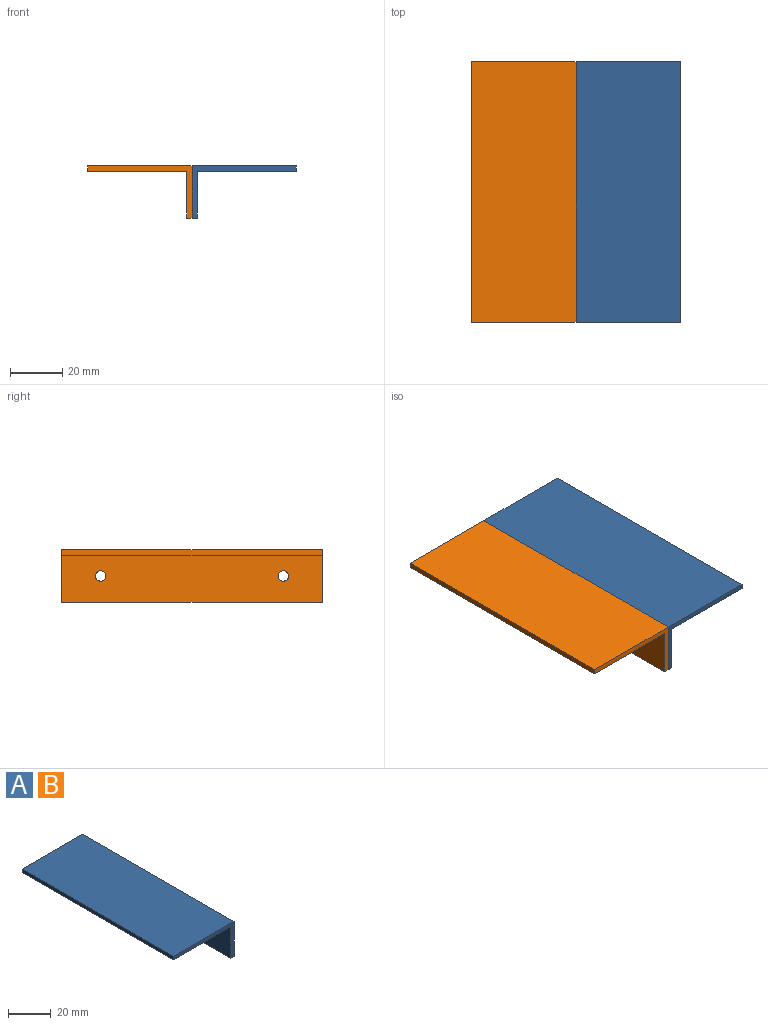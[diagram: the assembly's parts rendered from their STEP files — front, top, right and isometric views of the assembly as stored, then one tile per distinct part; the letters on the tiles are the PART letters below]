
ASSEMBLY  parts=2 mates=1
PART A: 10 faces, bbox 40x100x20 mm
  f0: plane 100x18mm, normal (-1,0,0), area 1774.9mm2, adj f3,f4,f6,f7,f8,f9
  f1: plane 100x20mm, normal (1,0,0), area 1974.9mm2, adj f4,f5,f6,f7,f8,f9
  f2: plane 100x2mm, normal (-1,0,0), area 200mm2, adj f3,f5,f6,f7
  f3: plane 100x38mm, normal (0,0,-1), area 3800mm2, adj f0,f2,f6,f7
  f4: plane 100x2mm, normal (0,0,-1), area 200mm2, adj f0,f1,f6,f7
  f5: plane 100x40mm, normal (0,0,1), area 4000mm2, adj f1,f2,f6,f7
  f6: plane 40x20mm, normal (0,-1,0), area 116mm2, adj f0,f1,f2,f3,f4,f5
  f7: plane 40x20mm, normal (0,1,0), area 116mm2, adj f0,f1,f2,f3,f4,f5
  f8: cylinder r=2mm len=4mm, axis (-1,0,0), area 25.1mm2, adj f0,f1
  f9: cylinder r=2mm len=4mm, axis (-1,0,0), area 25.1mm2, adj f0,f1
PART B: same geometry as A
PLACE A rot(axis=(0,0,1),180deg) t=(3.13,-3.97,16.18)mm
PLACE B t=(3.13,-3.97,16.18)mm
MATE fastened A.f1 <-> B.f1  axis (-1,0,0) through (3.13,-3.97,6.18)mm
